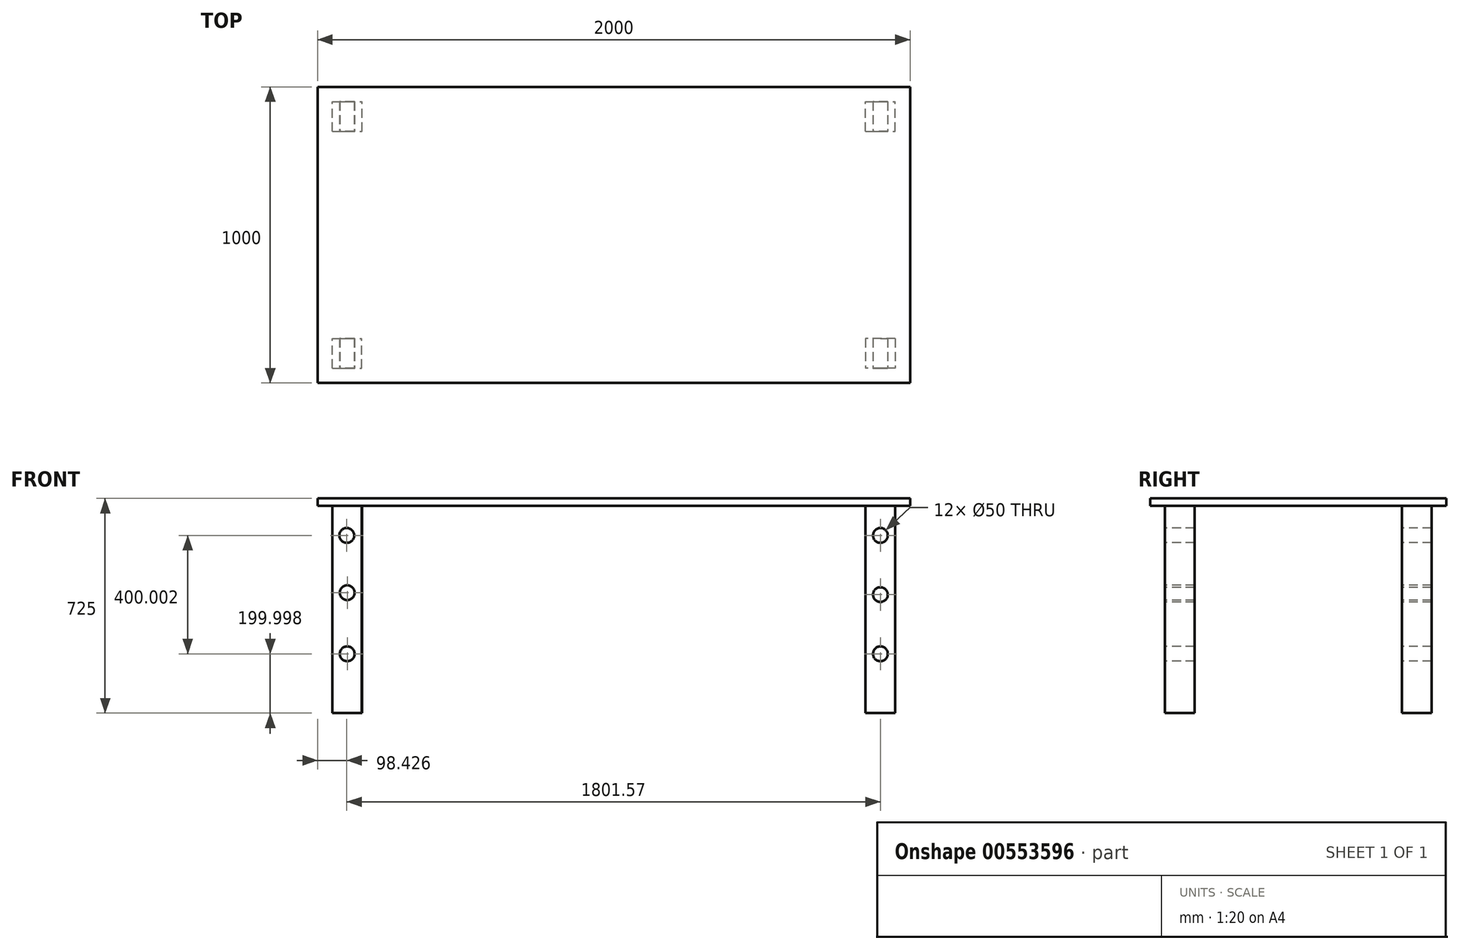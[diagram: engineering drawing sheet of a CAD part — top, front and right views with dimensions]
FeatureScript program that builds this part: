
annotation { "Feature Type Name" : "Feature", "Feature Type Description" : "" }
export const myFeature = defineFeature(function(context is Context, id is Id, definition is map)
    precondition{}
    {
        {
            var Q0;
            Q0=qCreatedBy(makeId("Top.planeOp"),FACE);
            var sketch = newSketch(context, id + "F0", { "sketchPlane" : qUnion([Q0])});
            skLineSegment(sketch, "E0.bottom", {"start": v(-1000, 437.12) * mm, "end": v(1000, 437.12) * mm});
            skLineSegment(sketch, "E0.top", {"start": v(-1000, -562.88) * mm, "end": v(1000, -562.88) * mm});
            skLineSegment(sketch, "E0.left", {"start": v(-1000, 437.12) * mm, "end": v(-1000, -562.88) * mm});
            skLineSegment(sketch, "E0.right", {"start": v(1000, 437.12) * mm, "end": v(1000, -562.88) * mm});
            skSolve(sketch);
        }
        {
            var Q0;
            Q0 = qSketchRegion(id + "F0", true);
            extrude(context, id + "F1", {"entities" : qUnion([Q0]), "depth" : 25 * mm, "offsetDistance" : 25 * mm});
        }
        {
            var Q0;
            Q0=makeQuery(id+"F1.opExtrude","CAP_FACE",FACE,{"disambiguationData":[OSD([sQuery(id+"F0.wireOp",EDGE,"E0.bottom"),sQuery(id+"F0.wireOp",EDGE,"E0.top"),sQuery(id+"F0.wireOp",EDGE,"E0.left"),sQuery(id+"F0.wireOp",EDGE,"E0.right")])],"isStart":true});
            var sketch = newSketch(context, id + "F2", { "sketchPlane" : qUnion([Q0])});
            skLineSegment(sketch, "E1.bottom", {"start": v(-950, 512.88) * mm, "end": v(-851.57, 512.88) * mm});
            skLineSegment(sketch, "E1.top", {"start": v(-950, 412.88) * mm, "end": v(-851.57, 412.88) * mm});
            skLineSegment(sketch, "E1.left", {"start": v(-950, 512.88) * mm, "end": v(-950, 412.88) * mm});
            skLineSegment(sketch, "E1.right", {"start": v(-851.57, 512.88) * mm, "end": v(-851.57, 412.88) * mm});
            skSolve(sketch);
        }
        {
            var Q0;
            Q0 = qSketchRegion(id + "F2", true);
            extrude(context, id + "F3", {"entities" : qUnion([Q0]), "operationType" : NewBodyOperationType.ADD, "depth" : 700 * mm, "offsetDistance" : 25 * mm});
        }
        {
            var Q0;
            Q0=makeQuery(id+"F1.opExtrude","CAP_FACE",FACE,{"disambiguationData":[OSD([sQuery(id+"F0.wireOp",EDGE,"E0.bottom"),sQuery(id+"F0.wireOp",EDGE,"E0.top"),sQuery(id+"F0.wireOp",EDGE,"E0.left"),sQuery(id+"F0.wireOp",EDGE,"E0.right")])],"isStart":true});
            var sketch = newSketch(context, id + "F4", { "sketchPlane" : qUnion([Q0])});
            skLineSegment(sketch, "E2.bottom", {"start": v(-950, -287.12) * mm, "end": v(-850, -287.12) * mm});
            skLineSegment(sketch, "E2.top", {"start": v(-950, -387.12) * mm, "end": v(-850, -387.12) * mm});
            skLineSegment(sketch, "E2.left", {"start": v(-950, -287.12) * mm, "end": v(-950, -387.12) * mm});
            skLineSegment(sketch, "E2.right", {"start": v(-850, -287.12) * mm, "end": v(-850, -387.12) * mm});
            skSolve(sketch);
        }
        {
            var Q0;
            Q0 = qSketchRegion(id + "F4", true);
            extrude(context, id + "F5", {"entities" : qUnion([Q0]), "operationType" : NewBodyOperationType.ADD, "depth" : 700 * mm, "offsetDistance" : 25 * mm});
        }
        {
            var Q0;
            Q0=makeQuery(id+"F1.opExtrude","CAP_FACE",FACE,{"disambiguationData":[OSD([sQuery(id+"F0.wireOp",EDGE,"E0.bottom"),sQuery(id+"F0.wireOp",EDGE,"E0.top"),sQuery(id+"F0.wireOp",EDGE,"E0.left"),sQuery(id+"F0.wireOp",EDGE,"E0.right")])],"isStart":true});
            var sketch = newSketch(context, id + "F6", { "sketchPlane" : qUnion([Q0])});
            skLineSegment(sketch, "E3.bottom", {"start": v(850, -287.12) * mm, "end": v(950, -287.12) * mm});
            skLineSegment(sketch, "E3.top", {"start": v(850, -387.12) * mm, "end": v(950, -387.12) * mm});
            skLineSegment(sketch, "E3.left", {"start": v(850, -287.12) * mm, "end": v(850, -387.12) * mm});
            skLineSegment(sketch, "E3.right", {"start": v(950, -287.12) * mm, "end": v(950, -387.12) * mm});
            skSolve(sketch);
        }
        {
            var Q0;
            Q0 = qSketchRegion(id + "F6", true);
            extrude(context, id + "F7", {"entities" : qUnion([Q0]), "operationType" : NewBodyOperationType.ADD, "depth" : 700 * mm, "offsetDistance" : 25 * mm});
        }
        {
            var Q0;
            Q0=makeQuery(id+"F1.opExtrude","CAP_FACE",FACE,{"disambiguationData":[OSD([sQuery(id+"F0.wireOp",EDGE,"E0.bottom"),sQuery(id+"F0.wireOp",EDGE,"E0.top"),sQuery(id+"F0.wireOp",EDGE,"E0.left"),sQuery(id+"F0.wireOp",EDGE,"E0.right")])],"isStart":true});
            var sketch = newSketch(context, id + "F8", { "sketchPlane" : qUnion([Q0])});
            skLineSegment(sketch, "E4.bottom", {"start": v(950, 412.88) * mm, "end": v(850, 412.88) * mm});
            skLineSegment(sketch, "E4.top", {"start": v(950, 512.88) * mm, "end": v(850, 512.88) * mm});
            skLineSegment(sketch, "E4.left", {"start": v(950, 412.88) * mm, "end": v(950, 512.88) * mm});
            skLineSegment(sketch, "E4.right", {"start": v(850, 412.88) * mm, "end": v(850, 512.88) * mm});
            skSolve(sketch);
        }
        {
            var Q0;
            Q0 = qSketchRegion(id + "F8", true);
            extrude(context, id + "F9", {"entities" : qUnion([Q0]), "operationType" : NewBodyOperationType.ADD, "depth" : 700 * mm, "offsetDistance" : 25 * mm});
        }
        {
            var Q0;
            Q0=makeQuery(id+"F3.opExtrude","SWEPT_FACE",FACE,{"disambiguationData":[OSD([sQuery(id+"F2.wireOp",EDGE,"E1.bottom")])]});
            var sketch = newSketch(context, id + "F10", { "sketchPlane" : qUnion([Q0])});
            skCircle(sketch, "E5", {"center": v(-900, -500) * mm, "radius": 25 * mm});
            skSolve(sketch);
        }
        {
            var Q0;
            Q0=sQuery(id+"F10.wireOp",VERTEX,"E5.center");
            var Q1;
            Q1=makeQuery(id+"F1.opExtrude","SWEPT_BODY",BODY,{"disambiguationData":[OSD([sQuery(id+"F0.wireOp",EDGE,"E0.bottom"),sQuery(id+"F0.wireOp",EDGE,"E0.top"),sQuery(id+"F0.wireOp",EDGE,"E0.left"),sQuery(id+"F0.wireOp",EDGE,"E0.right")])]});
            hole(context, id + "F11", {"style" : HoleStyle.SIMPLE, "endStyle" : HoleEndStyle.THROUGH, "holeDiameter" : 50 * mm, "isTappedThrough" : true, "tappedDepth" : 12 * mm, "tapClearance" : 3, "locations" : qUnion([Q0]), "scope" : qUnion([Q1])});
        }
        {
            var Q0;
            Q0=makeQuery(id+"F3.opExtrude","SWEPT_FACE",FACE,{"disambiguationData":[OSD([sQuery(id+"F2.wireOp",EDGE,"E1.bottom")])]});
            var sketch = newSketch(context, id + "F12", { "sketchPlane" : qUnion([Q0])});
            skCircle(sketch, "E6", {"center": v(-900, -293.51) * mm, "radius": 25 * mm});
            skSolve(sketch);
        }
        {
            var Q0;
            Q0=sQuery(id+"F12.wireOp",VERTEX,"E6.center");
            var Q1;
            Q1=makeQuery(id+"F1.opExtrude","SWEPT_BODY",BODY,{"disambiguationData":[OSD([sQuery(id+"F0.wireOp",EDGE,"E0.bottom"),sQuery(id+"F0.wireOp",EDGE,"E0.top"),sQuery(id+"F0.wireOp",EDGE,"E0.left"),sQuery(id+"F0.wireOp",EDGE,"E0.right")])]});
            hole(context, id + "F13", {"style" : HoleStyle.SIMPLE, "endStyle" : HoleEndStyle.THROUGH, "holeDiameter" : 50 * mm, "isTappedThrough" : true, "tappedDepth" : 12 * mm, "tapClearance" : 3, "locations" : qUnion([Q0]), "scope" : qUnion([Q1])});
        }
        {
            var Q0;
            Q0=makeQuery(id+"F3.opExtrude","SWEPT_FACE",FACE,{"disambiguationData":[OSD([sQuery(id+"F2.wireOp",EDGE,"E1.bottom")])]});
            var sketch = newSketch(context, id + "F14", { "sketchPlane" : qUnion([Q0])});
            skCircle(sketch, "E7", {"center": v(-901.57, -100) * mm, "radius": 19.5 * mm});
            skSolve(sketch);
        }
        {
            var Q0;
            Q0=sQuery(id+"F14.wireOp",VERTEX,"E7.center");
            var Q1;
            Q1=makeQuery(id+"F1.opExtrude","SWEPT_BODY",BODY,{"disambiguationData":[OSD([sQuery(id+"F0.wireOp",EDGE,"E0.bottom"),sQuery(id+"F0.wireOp",EDGE,"E0.top"),sQuery(id+"F0.wireOp",EDGE,"E0.left"),sQuery(id+"F0.wireOp",EDGE,"E0.right")])]});
            hole(context, id + "F15", {"style" : HoleStyle.SIMPLE, "endStyle" : HoleEndStyle.THROUGH, "holeDiameter" : 50 * mm, "isTappedThrough" : true, "tappedDepth" : 12 * mm, "tapClearance" : 3, "locations" : qUnion([Q0]), "scope" : qUnion([Q1])});
        }
        {
            var Q0;
            Q0=makeQuery(id+"F9.opExtrude","SWEPT_FACE",FACE,{"disambiguationData":[OSD([sQuery(id+"F8.wireOp",EDGE,"E4.top")])]});
            var sketch = newSketch(context, id + "F16", { "sketchPlane" : qUnion([Q0])});
            skCircle(sketch, "E8", {"center": v(900, -500) * mm, "radius": 19.42 * mm});
            skSolve(sketch);
        }
        {
            var Q0;
            Q0=sQuery(id+"F16.wireOp",VERTEX,"E8.center");
            var Q1;
            Q1=makeQuery(id+"F1.opExtrude","SWEPT_BODY",BODY,{"disambiguationData":[OSD([sQuery(id+"F0.wireOp",EDGE,"E0.bottom"),sQuery(id+"F0.wireOp",EDGE,"E0.top"),sQuery(id+"F0.wireOp",EDGE,"E0.left"),sQuery(id+"F0.wireOp",EDGE,"E0.right")])]});
            hole(context, id + "F17", {"style" : HoleStyle.SIMPLE, "endStyle" : HoleEndStyle.THROUGH, "holeDiameter" : 50 * mm, "isTappedThrough" : true, "tappedDepth" : 12 * mm, "tapClearance" : 3, "locations" : qUnion([Q0]), "scope" : qUnion([Q1])});
        }
        {
            var Q0;
            Q0=makeQuery(id+"F9.opExtrude","SWEPT_FACE",FACE,{"disambiguationData":[OSD([sQuery(id+"F8.wireOp",EDGE,"E4.top")])]});
            var sketch = newSketch(context, id + "F18", { "sketchPlane" : qUnion([Q0])});
            skCircle(sketch, "E9", {"center": v(900, -300) * mm, "radius": 18.54 * mm});
            skSolve(sketch);
        }
        {
            var Q0;
            Q0=sQuery(id+"F18.wireOp",VERTEX,"E9.center");
            var Q1;
            Q1=makeQuery(id+"F1.opExtrude","SWEPT_BODY",BODY,{"disambiguationData":[OSD([sQuery(id+"F0.wireOp",EDGE,"E0.bottom"),sQuery(id+"F0.wireOp",EDGE,"E0.top"),sQuery(id+"F0.wireOp",EDGE,"E0.left"),sQuery(id+"F0.wireOp",EDGE,"E0.right")])]});
            hole(context, id + "F19", {"style" : HoleStyle.SIMPLE, "endStyle" : HoleEndStyle.THROUGH, "holeDiameter" : 50 * mm, "isTappedThrough" : true, "tappedDepth" : 12 * mm, "tapClearance" : 3, "locations" : qUnion([Q0]), "scope" : qUnion([Q1])});
        }
        {
            var Q0;
            Q0=makeQuery(id+"F9.opExtrude","SWEPT_FACE",FACE,{"disambiguationData":[OSD([sQuery(id+"F8.wireOp",EDGE,"E4.top")])]});
            var sketch = newSketch(context, id + "F20", { "sketchPlane" : qUnion([Q0])});
            skCircle(sketch, "E10", {"center": v(900, -100) * mm, "radius": 20.32 * mm});
            skSolve(sketch);
        }
        {
            var Q0;
            Q0=sQuery(id+"F20.wireOp",VERTEX,"E10.center");
            var Q1;
            Q1=makeQuery(id+"F1.opExtrude","SWEPT_BODY",BODY,{"disambiguationData":[OSD([sQuery(id+"F0.wireOp",EDGE,"E0.bottom"),sQuery(id+"F0.wireOp",EDGE,"E0.top"),sQuery(id+"F0.wireOp",EDGE,"E0.left"),sQuery(id+"F0.wireOp",EDGE,"E0.right")])]});
            hole(context, id + "F21", {"style" : HoleStyle.SIMPLE, "endStyle" : HoleEndStyle.THROUGH, "holeDiameter" : 50 * mm, "isTappedThrough" : true, "tappedDepth" : 12 * mm, "tapClearance" : 3, "locations" : qUnion([Q0]), "scope" : qUnion([Q1])});
        }
    });
